# Revit family: Drinking_Fountain-Haws_Corporation-Pedestal_3300
name_source: partatom
category: Plumbing Fixtures
revit_build: Autodesk Revit Architecture 2015 (Build: 20140606_1530(x64)
units: mm (PartAtom-declared; Revit-internal decimal feet)

## types (3) — shared parameters
Assembly Code = D2010810
Back Panel = 11"
Bowl = Metal - Haws Corporation - Stainless Steel - With Bead
Bubbler = Metal - Haws Corporation - Polished Chrome - 5703M
Cost Note = For Cost information please visit the Resource tab in the Product Page URL
Flow = 0.00 GPM
Keynote = 15410.A1
Manufacturer = Haws Corporation
Product Page URL = http://www.hawsco.com
Series = Haws heavy-duty pedestal drinking fountains
URL = http://www.hawsco.com
Version = 2014-v2.0a

## per-type parameters (varying)
| type | Bowl Height | CWFU | Cost | Description | HW Connection | HWFU | Pedestal | Product Documentation Link | Sanitary Radius | Supply Radius | To Spot Outlet | Type Comments | Vent Connection | WFU | Waste Connection |
| 3300 | 27" | 1 | $0.00 | The "Hi-Lo" barrier free design of the 3300 allows the square pedestal to be placed securely in multiple locations | No | 1 | Metal - Haws Corporation - Green Powder Coated Finish | https://www.hawsco.com | 1/2" | 0" | 35 1/2" | Include an 11 gauge galvanized substrate steel pedestal with green powder-coating | No | 1 | Yes |
| 3300FR | 23 1/2" | 2 | $3800.00 | The "Hi-Lo" barrier free design of the 3300FR allows the square pedestal to be placed securely in multiple locations | No | 2 | Metal - Haws Corporation - Green Powder Coated Finish | http://www.hawsco.com | 1" | 1/2" | 0" | Use a freeze-resistant valve assembly to provide year round operation | Yes | 2 | No |
| 3300G | 23 1/2" | 3 | $3600.00 | Barrier-free capabilities combined with its ease of use allows for
a number of installation location possibilities | Yes | 3 | Metal - Haws Corporation - Galvanized Steel | https://www.hawsco.com | 1" | 1/2" | 0" | Include an 11 gauge galvanized steel pedestal | No | 3 | Yes |

note: column(s) folded — value = type name in every type: Model

## geometry (parser evidence)
native form markers: Blend x43, Sweep x3
no freeform markers — native parametric forms only
